# Revit family: LAC-LP
name_source: partatom
category: Lighting Fixtures
revit_build: Autodesk Revit 2014 (Build: 20130709_2115(x64)
units: mm (PartAtom-declared; Revit-internal decimal feet)

## types (2) — shared parameters
Color Filter = 16777215
Comments = his model is for use in spatial massing and rendering. Please contact LightArt for pick-point placement and installation details.
Diffuser = White Opal Acrylic
Dimming Compatibility = 0-10v
Dimming Lamp Color Temperature Shift = <None>
Driver = 24v
Emit from Line Length = 1' - 8"
HARDWARE = Matte silver canopy mounts to round
junction box (provided by others)
Silver power cord to canopy
Adjustable 12”-96” suspension
Hardware = <By Category>
Height = 1' - 11 1/2"
Height From Face = 4' - 0"
Input = 120v-277v
LIGHTING = (1) 19W E26 Base CFL
3500K 82 CRI light source
120V standard; 277V option available
LED option available
Dimming option available
UL Labeled
Light = <By Category>
Light Source Distance = 4' - 8"
Light Source Symbol Size = 0' - 5"
Manufacturer = LightArt
Model = LAC-LP
Plastic Rivet = <By Category>
STANDARDS = Customizable dimensions, materials,
hardware and lighting
4-6 week lead time
10,000+ 3form material options
1 year limited warranty
Pricing based on maximum sheet yield and
PGB material
Contact for custom pricing

hardware and lighting

4-6 week lead time

10,000+ 3form material options

1 year limited warranty

Pricing based on maximum sheet yield and

PGB material

Contact for custom pricing
Shade = 3form Varia Ecoresin

## per-type parameters (varying)
| type | 9" x 14" | 9" x 24" |
| LP-9" x 24" | No | Yes |
| LP-9" x14" | Yes | No |

## geometry (parser evidence)
native form markers: Blend x2, Sweep x9
no freeform markers — native parametric forms only
